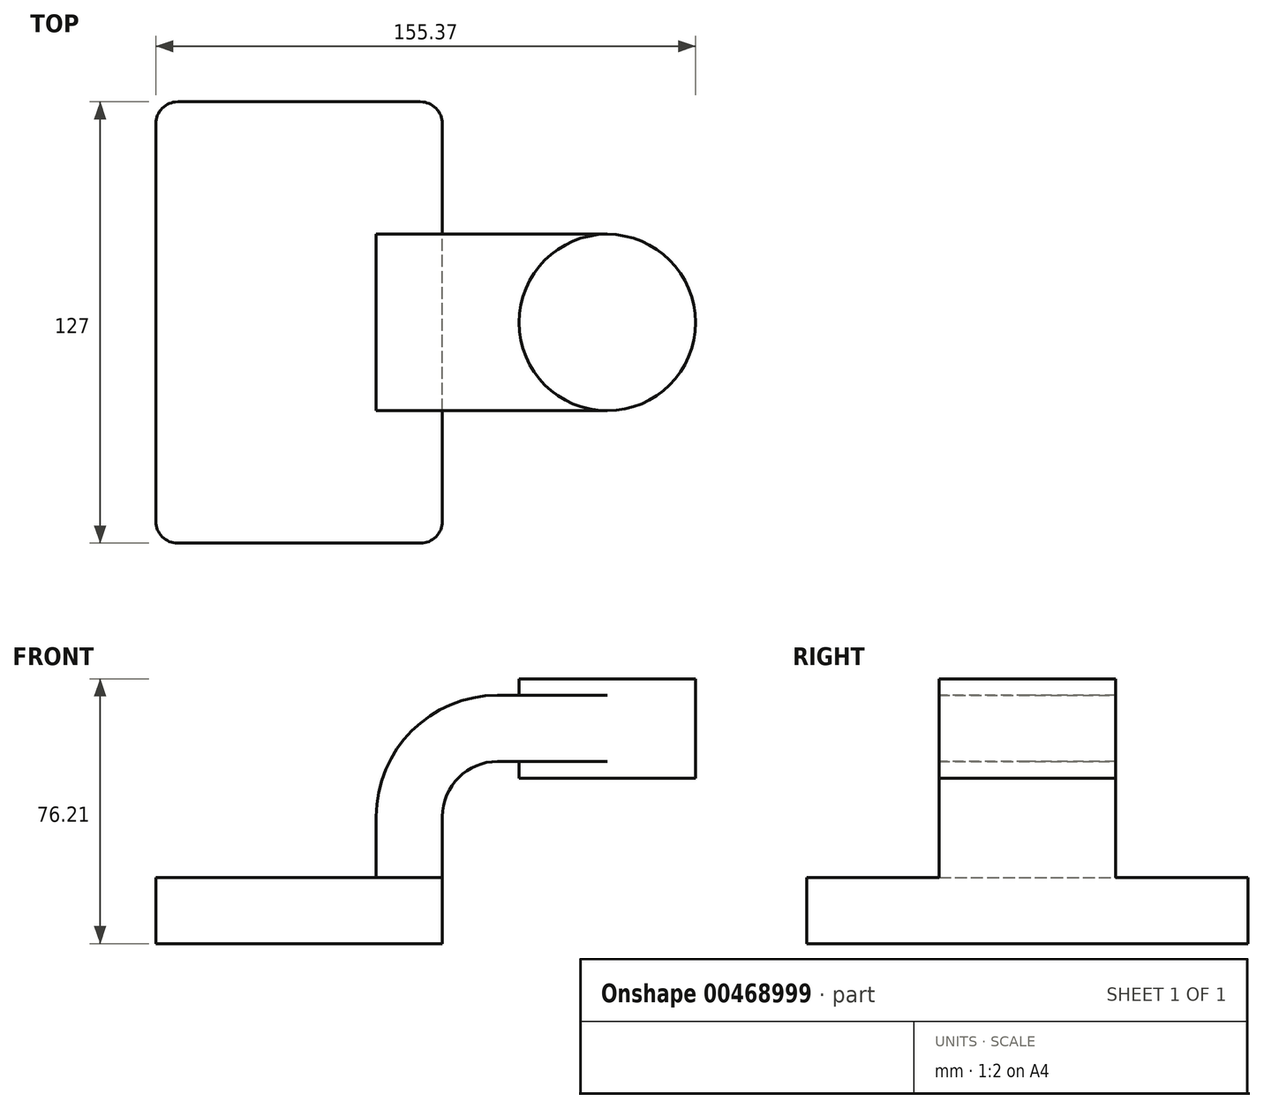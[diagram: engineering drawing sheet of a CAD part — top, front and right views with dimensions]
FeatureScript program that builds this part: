
annotation { "Feature Type Name" : "Feature", "Feature Type Description" : "" }
export const myFeature = defineFeature(function(context is Context, id is Id, definition is map)
    precondition{}
    {
        {
            var Q0;
            Q0=qCreatedBy(makeId("Front.planeOp"),FACE);
            var sketch = newSketch(context, id + "F0", { "sketchPlane" : qUnion([Q0])});
            skLineSegment(sketch, "E0.bottom", {"start": v(-41.27, -9.52) * mm, "end": v(41.28, -9.52) * mm});
            skLineSegment(sketch, "E0.top", {"start": v(-41.28, 9.53) * mm, "end": v(41.28, 9.53) * mm});
            skLineSegment(sketch, "E0.left", {"start": v(-41.27, -9.52) * mm, "end": v(-41.28, 9.53) * mm});
            skLineSegment(sketch, "E0.right", {"start": v(41.28, -9.52) * mm, "end": v(41.28, 9.53) * mm});
            skPoint(sketch, "E0.middle", {"position": v(0, 0) * mm});
            skLineSegment(sketch, "E1.bottom", {"start": v(114.1, 38.1) * mm, "end": v(63.3, 38.1) * mm});
            skLineSegment(sketch, "E1.top", {"start": v(114.1, 66.68) * mm, "end": v(63.3, 66.68) * mm});
            skLineSegment(sketch, "E1.left", {"start": v(114.1, 38.1) * mm, "end": v(114.1, 66.68) * mm});
            skLineSegment(sketch, "E1.right", {"start": v(63.3, 38.1) * mm, "end": v(63.3, 66.67) * mm});
            skPoint(sketch, "E1.middle", {"position": v(88.7, 52.39) * mm});
            skLineSegment(sketch, "E2", {"start": v(41.27, 9.53) * mm, "end": v(41.27, 27) * mm});
            skArc(sketch, "E3", {"start": v(41.28, 27) * mm, "mid": v(45.92, 38.23) * mm, "end": v(57.15, 42.88) * mm});
            skLineSegment(sketch, "E4", {"start": v(57.15, 42.88) * mm, "end": v(88.7, 42.88) * mm});
            skLineSegment(sketch, "E5.0", {"start": v(57.15, 61.93) * mm, "end": v(88.7, 61.93) * mm});
            skArc(sketch, "E5.1", {"start": v(22.23, 27) * mm, "mid": v(32.45, 51.7) * mm, "end": v(57.15, 61.93) * mm});
            skLineSegment(sketch, "E5.2", {"start": v(22.22, 9.53) * mm, "end": v(22.22, 27) * mm});
            skLineSegment(sketch, "E6", {"start": v(88.7, 42.88) * mm, "end": v(88.7, 61.93) * mm});
            skFitSpline(sketch, "E7", {"points": [v(-41.28, 9.52) * mm, v(57.15, 61.93) * mm], "startDerivative": vector(25.1, 67.3) * mm, "endDerivative": vector(133.95, -27.8) * mm});
            skLineSegment(sketch, "E8", {"start": v(88.7, 38.1) * mm, "end": v(88.7, 66.68) * mm});
            skSolve(sketch);
        }
        {
            var Q0;
            Q0=makeQuery(id+"F0.imprint","IMPRINT",FACE,{"disambiguationData":[TD([[makeQuery(id+"F0.imprint","IMPRINT",EDGE,{"derivedFrom":sQuery(id+"F0.wireOp",EDGE,"E0.bottom")}),1.0]])]});
            extrude(context, id + "F1", {"entities" : qUnion([Q0]), "endBound" : BoundingType.SYMMETRIC, "depth" : 127 * mm});
        }
        {
            var Q0;
            {var subQ5=sQuery(id+"F0.wireOp",EDGE,"E6");Q0=makeQuery(id+"F0.imprint","IMPRINT",FACE,{"disambiguationData":[TD([[makeQuery(id+"F0.imprint","IMPRINT",EDGE,{"derivedFrom":subQ5}),1.0]])]});}
            var Q1;
            {var subQ0=sQuery(id+"F0.wireOp",EDGE,"E2");Q1=makeQuery(id+"F0.imprint","IMPRINT",FACE,{"disambiguationData":[TD([[makeQuery(id+"F0.imprint","IMPRINT",EDGE,{"derivedFrom":subQ0}),1.0]])]});}
            var Q2;
            {var subQ0=sQuery(id+"F0.wireOp",EDGE,"E4");var subQ1=sQuery(id+"F0.wireOp",EDGE,"E1.right");var subQ2=makeQuery(id+"F0.imprint","INTERSECT",VERTEX,{"derivedFrom":[subQ1,subQ0]});Q2=makeQuery(id+"F0.imprint","IMPRINT",FACE,{"disambiguationData":[TD([[makeQuery(id+"F0.imprint","IMPRINT",EDGE,{"disambiguationData":[TD([[subQ2,-1.0]])],"derivedFrom":subQ1}),-1.0]])]});}
            extrude(context, id + "F2", {"entities" : qUnion([Q0, Q1, Q2]), "operationType" : NewBodyOperationType.ADD, "endBound" : BoundingType.SYMMETRIC, "depth" : 50.8 * mm});
        }
        {
            var Q0;
            Q0=makeQuery(id+"F0.imprint","IMPRINT",FACE,{"disambiguationData":[TD([[makeQuery(id+"F0.imprint","IMPRINT",EDGE,{"derivedFrom":sQuery(id+"F0.wireOp",EDGE,"E5.1")}),1.0]])]});
            extrude(context, id + "F3", {"entities" : qUnion([Q0]), "operationType" : NewBodyOperationType.ADD, "endBound" : BoundingType.SYMMETRIC, "depth" : 15.88 * mm});
        }
        {
            var Q0;
            {var subQ0=sQuery(id+"F0.wireOp",EDGE,"E1.left");Q0=makeQuery(id+"F0.imprint","IMPRINT",FACE,{"disambiguationData":[TD([[makeQuery(id+"F0.imprint","IMPRINT",EDGE,{"derivedFrom":subQ0}),1.0]])]});}
            var Q1;
            Q1=sQuery(id+"F0.wireOp",EDGE,"E8");
            revolve(context, id + "F4", {"operationType" : NewBodyOperationType.ADD, "entities" : qUnion([Q0]), "axis" : qUnion([Q1]), "revolveType" : RevolveType.FULL});
        }
        {
            var Q0;
            Q0=makeQuery(id+"F1.opExtrude","CAP_EDGE",EDGE,{"disambiguationData":[OSD([sQuery(id+"F0.wireOp",EDGE,"E0.right")])],"isStart":true});
            var Q1;
            Q1=makeQuery(id+"F1.opExtrude","CAP_EDGE",EDGE,{"disambiguationData":[OSD([sQuery(id+"F0.wireOp",EDGE,"E0.left")])],"isStart":false});
            var Q2;
            Q2=makeQuery(id+"F1.opExtrude","CAP_EDGE",EDGE,{"disambiguationData":[OSD([sQuery(id+"F0.wireOp",EDGE,"E0.left")])],"isStart":true});
            var Q3;
            Q3=makeQuery(id+"F1.opExtrude","CAP_EDGE",EDGE,{"disambiguationData":[OSD([sQuery(id+"F0.wireOp",EDGE,"E0.right")])],"isStart":false});
            fillet(context, id + "F5", {"entities" : qUnion([Q0, Q1, Q2, Q3]), "radius" : 6.35 * mm, "tangentPropagation" : true, "allowEdgeOverflow" : false});
        }
    });
